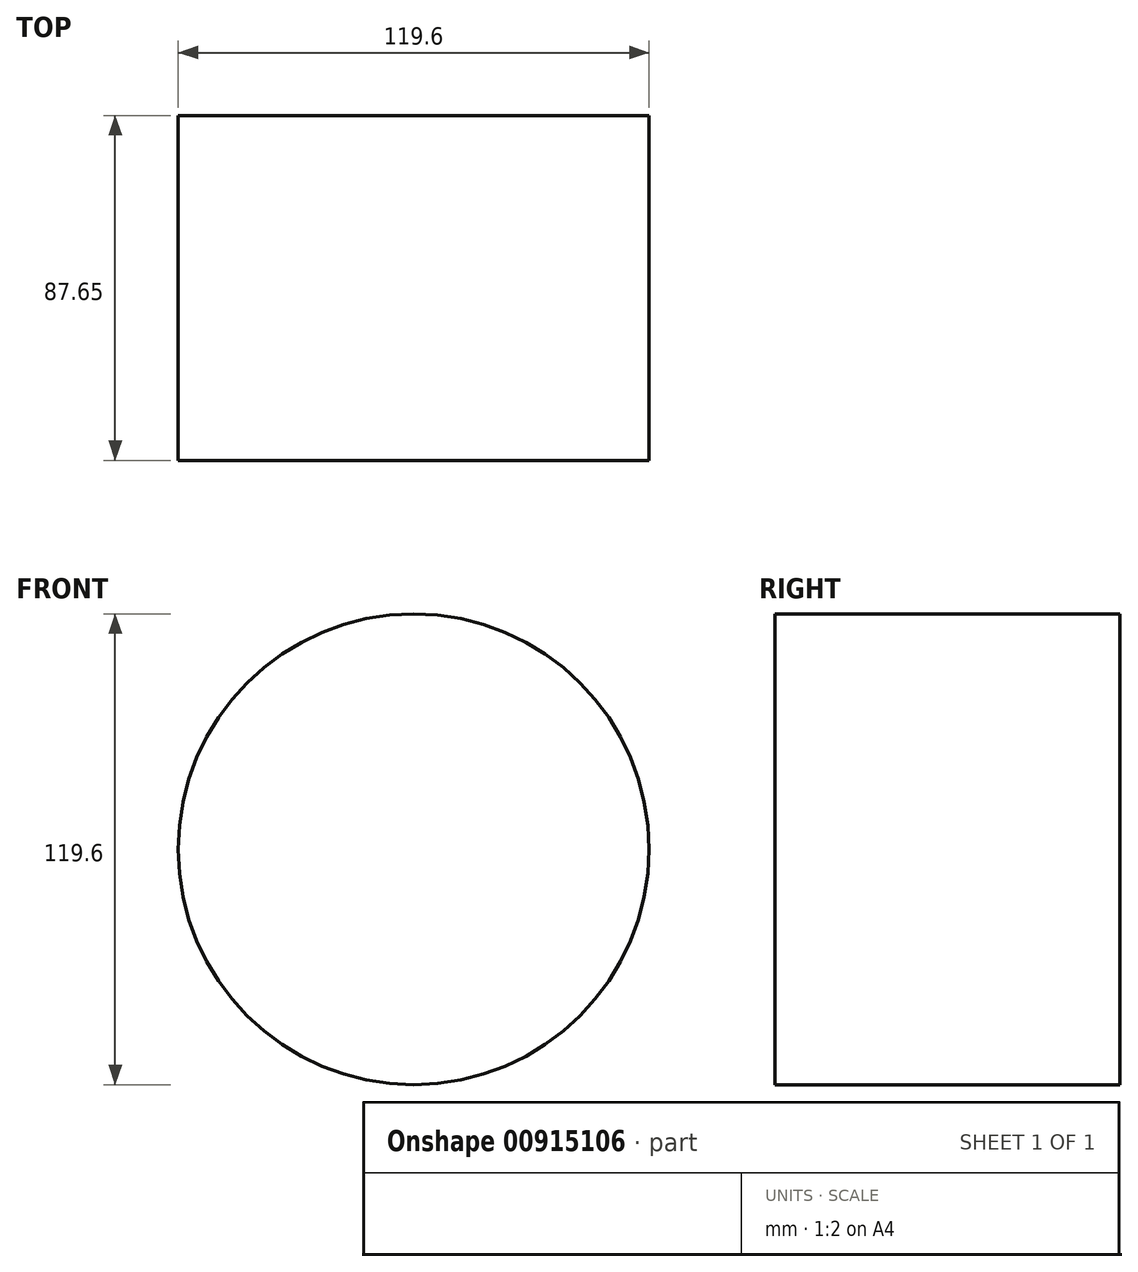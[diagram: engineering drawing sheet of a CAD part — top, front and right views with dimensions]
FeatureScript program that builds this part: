
annotation { "Feature Type Name" : "Feature", "Feature Type Description" : "" }
export const myFeature = defineFeature(function(context is Context, id is Id, definition is map)
    precondition{}
    {
        {
            var Q0;
            Q0=qCreatedBy(makeId("Front.planeOp"),FACE);
            var sketch = newSketch(context, id + "F0", { "sketchPlane" : qUnion([Q0])});
            skCircle(sketch, "E0", {"center": v(0, 0) * mm, "radius": 59.8 * mm});
            skSolve(sketch);
        }
        {
            var Q0;
            Q0 = qSketchRegion(id + "F0", true);
            extrude(context, id + "F1", {"entities" : qUnion([Q0]), "depth" : 87.65 * mm, "offsetDistance" : 25.4 * mm});
        }
    });
